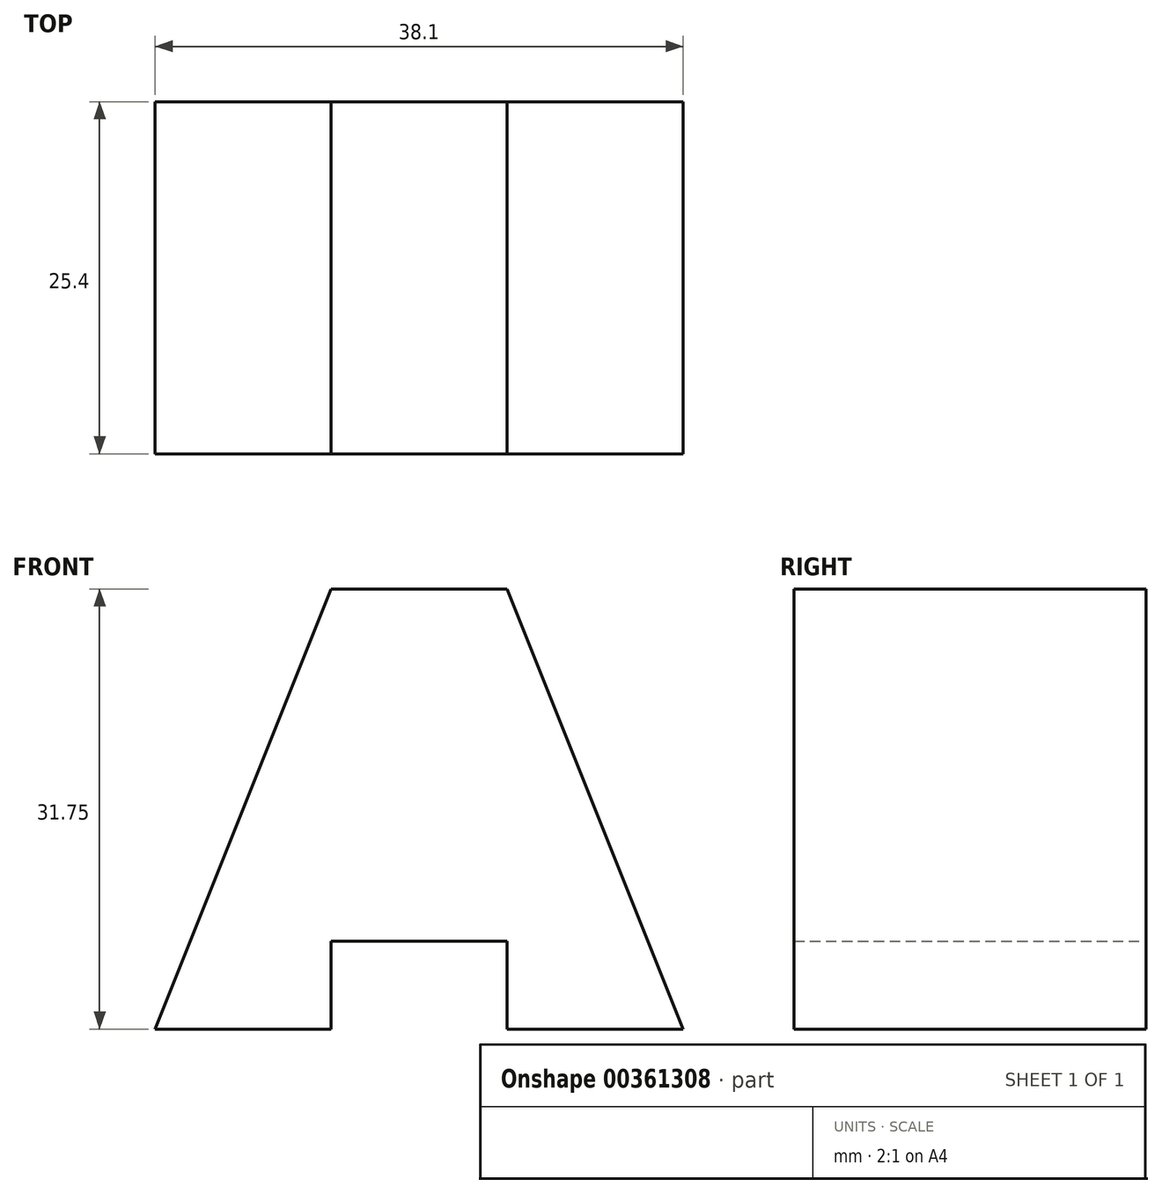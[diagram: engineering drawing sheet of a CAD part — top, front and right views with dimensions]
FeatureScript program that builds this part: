
annotation { "Feature Type Name" : "Feature", "Feature Type Description" : "" }
export const myFeature = defineFeature(function(context is Context, id is Id, definition is map)
    precondition{}
    {
        {
            var Q0;
            Q0=qCreatedBy(makeId("Front.planeOp"),FACE);
            var sketch = newSketch(context, id + "F0", { "sketchPlane" : qUnion([Q0])});
            skLineSegment(sketch, "E0", {"start": v(0, 0) * mm, "end": v(12.7, 0) * mm});
            skLineSegment(sketch, "E1", {"start": v(12.7, 0) * mm, "end": v(12.7, 6.35) * mm});
            skLineSegment(sketch, "E2", {"start": v(12.7, 6.35) * mm, "end": v(25.4, 6.35) * mm});
            skLineSegment(sketch, "E3", {"start": v(25.4, 6.35) * mm, "end": v(25.4, 0) * mm});
            skLineSegment(sketch, "E4", {"start": v(25.4, 0) * mm, "end": v(38.1, 0) * mm});
            skLineSegment(sketch, "E5", {"start": v(38.1, 0) * mm, "end": v(25.4, 31.75) * mm});
            skLineSegment(sketch, "E6", {"start": v(25.4, 31.75) * mm, "end": v(12.7, 31.75) * mm});
            skLineSegment(sketch, "E7", {"start": v(12.7, 31.75) * mm, "end": v(0, 0) * mm});
            skLineSegment(sketch, "E8", {"start": v(25.4, 0) * mm, "end": v(25.4, 31.75) * mm});
            skSolve(sketch);
        }
        {
            var Q0;
            Q0 = qSketchRegion(id + "F0", true);
            extrude(context, id + "F1", {"entities" : qUnion([Q0]), "depth" : 25.4 * mm});
        }
    });
